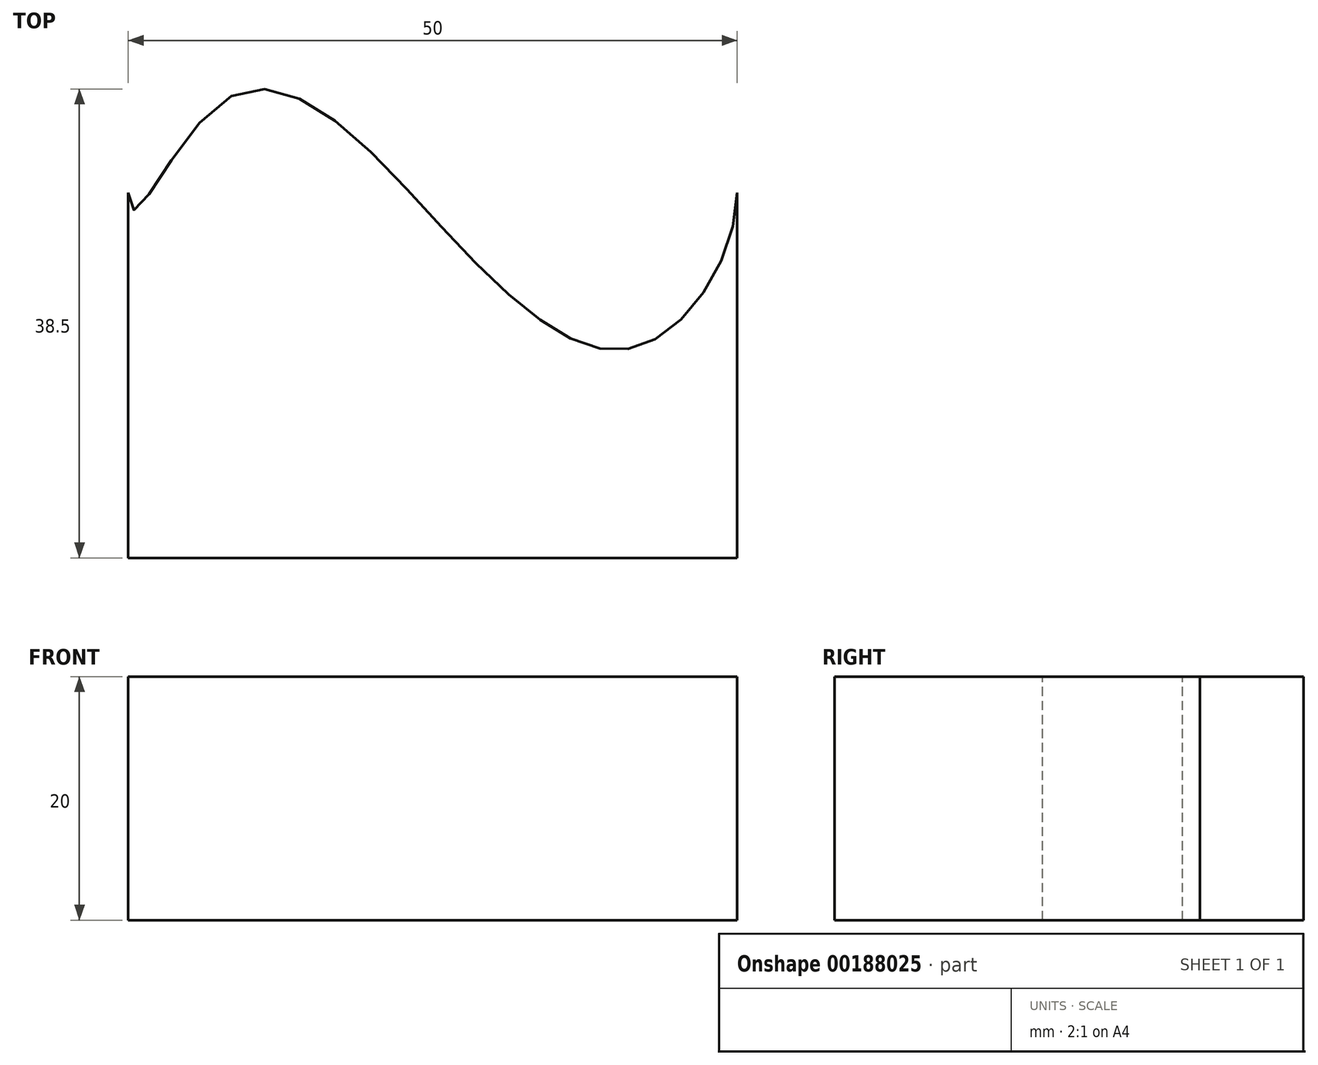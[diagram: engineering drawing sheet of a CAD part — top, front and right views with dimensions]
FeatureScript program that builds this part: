
annotation { "Feature Type Name" : "Feature", "Feature Type Description" : "" }
export const myFeature = defineFeature(function(context is Context, id is Id, definition is map)
    precondition{}
    {
        {
            var Q0;
            Q0=qCreatedBy(makeId("Top.planeOp"),FACE);
            var sketch = newSketch(context, id + "F0", { "sketchPlane" : qUnion([Q0])});
            skLineSegment(sketch, "E0", {"start": v(-25, 25) * mm, "end": v(-25, -5) * mm});
            skLineSegment(sketch, "E1", {"start": v(-25, -5) * mm, "end": v(25, -5) * mm});
            skLineSegment(sketch, "E2", {"start": v(25, -5) * mm, "end": v(25, 25) * mm});
            skFitSpline(sketch, "E3", {"points": [v(-25, 25) * mm, v(-17.4, 32.39) * mm, v(2.42, 20.38) * mm, v(17.08, 12.42) * mm, v(25, 25) * mm], "startDerivative": vector(0, -73.75) * mm, "endDerivative": vector(0, 62.29) * mm});
            skSolve(sketch);
        }
        {
            var Q0;
            Q0 = qSketchRegion(id + "F0", true);
            extrude(context, id + "F1", {"entities" : qUnion([Q0]), "depth" : 20 * mm});
        }
    });
